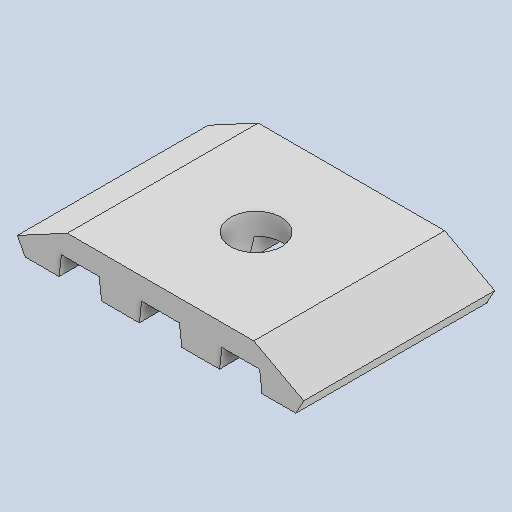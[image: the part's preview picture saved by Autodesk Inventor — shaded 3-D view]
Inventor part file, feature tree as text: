
AUTODESK INVENTOR PART (.ipt)
format: ipt  version: 2022 (Build 260153000, 153)  size: 97,280 bytes
history: native  units: in
note: dims shown in document units (in); Inventor stores cm internally (conversion verified against a paired STEP export)
features: hole x1
ambient origin geometry x8: Origin, YZ Plane, XZ Plane, XY Plane, X Axis, Y Axis, Z Axis, Center Point
bodies: Solid1 (feature_tree)
feature tree (1):
  hole  "Hole1"  [1 undecoded]
note: 1 required parameter value undecoded (feature->parameter linkage not recoverable at this tier; creation-order binding heuristic only, values carry confidence <= 0.55)
